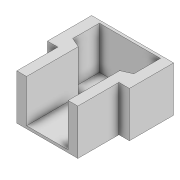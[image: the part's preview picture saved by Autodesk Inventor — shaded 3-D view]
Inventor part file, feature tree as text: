
AUTODESK INVENTOR PART (.ipt)
format: ipt  version: 2021 (Build 250183000, 183)  size: 137,728 bytes
history: native  units: in
note: dims shown in document units (in); Inventor stores cm internally (conversion verified against a paired STEP export)
features: extrude x3, sketch x3, projected_geometry x3
ambient origin geometry x8: Origin, YZ Plane, XZ Plane, XY Plane, X Axis, Y Axis, Z Axis, Center Point
bodies: Solid1 (feature_tree)
feature tree (9):
  extrude  "Extrusion1"  Depth=0.0625in TaperAngle=0.0deg
  extrude  "Extrusion2"  Depth=2.0in
  extrude  "Extrusion4"  [1 undecoded]
  sketch  "Sketch1"  dims[d0=1.0in d1=0.0in d2=0.0625in d3=0.0in]
  sketch  "Sketch2"  dims[d8=0.0625in d9=0.0in d10=2.0in]
  projected_geometry  "Projected Loop1"
  projected_geometry  "Projected Loop2"
  sketch  "Sketch4"  dims[d11=1.0in]
  projected_geometry  "Projected Loop4"
note: 1 required parameter value undecoded (feature->parameter linkage not recoverable at this tier; creation-order binding heuristic only, values carry confidence <= 0.55)
